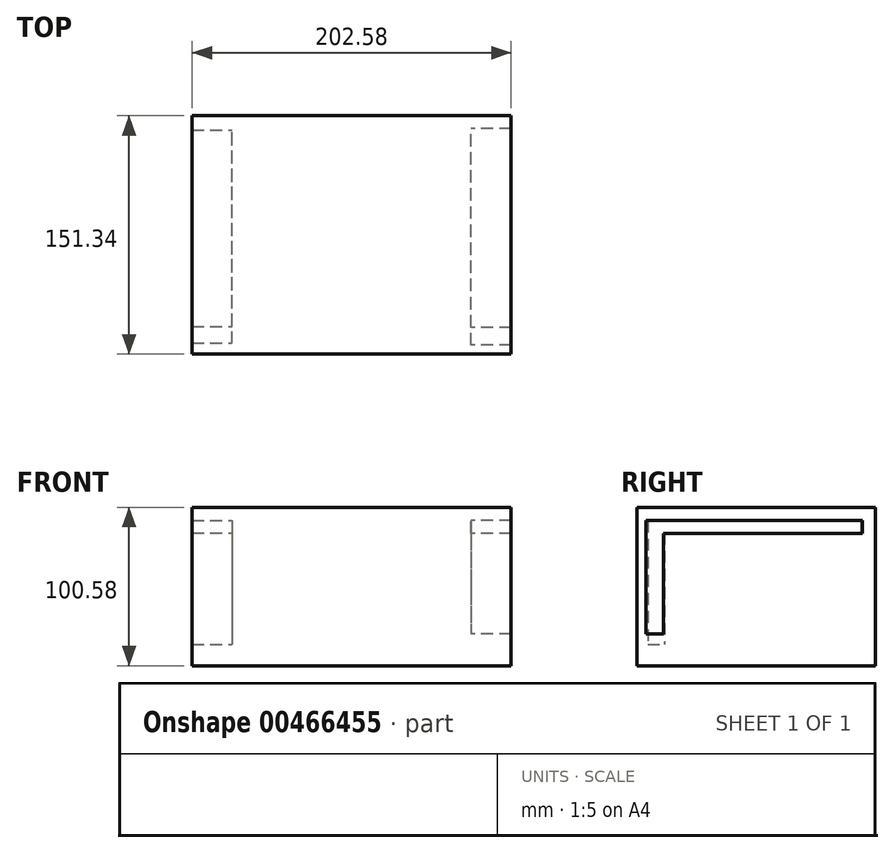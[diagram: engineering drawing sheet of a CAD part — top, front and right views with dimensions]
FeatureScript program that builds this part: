
annotation { "Feature Type Name" : "Feature", "Feature Type Description" : "" }
export const myFeature = defineFeature(function(context is Context, id is Id, definition is map)
    precondition{}
    {
        {
            var Q0;
            Q0=qCreatedBy(makeId("Top.planeOp"),FACE);
            var sketch = newSketch(context, id + "F0", { "sketchPlane" : qUnion([Q0])});
            skLineSegment(sketch, "E0.bottom", {"start": v(-76.71, -74.24) * mm, "end": v(75.07, -74.24) * mm});
            skLineSegment(sketch, "E0.top", {"start": v(-76.71, 77.1) * mm, "end": v(75.07, 77.1) * mm});
            skLineSegment(sketch, "E0.left", {"start": v(-76.71, -74.24) * mm, "end": v(-76.71, 77.1) * mm});
            skLineSegment(sketch, "E0.right", {"start": v(75.07, -74.24) * mm, "end": v(75.07, 77.1) * mm});
            skSolve(sketch);
        }
        {
            var Q0;
            Q0=makeQuery(id+"F0.imprint","IMPRINT",FACE,{"disambiguationData":[TD([[makeQuery(id+"F0.imprint","IMPRINT",EDGE,{"derivedFrom":sQuery(id+"F0.wireOp",EDGE,"E0.bottom")}),1.0]])]});
            extrude(context, id + "F1", {"entities" : qUnion([Q0]), "depth" : 100.58 * mm, "offsetDistance" : 25.4 * mm});
        }
        {
            var Q0;
            Q0=makeQuery(id+"F1.opExtrude","SWEPT_FACE",FACE,{"disambiguationData":[OSD([sQuery(id+"F0.wireOp",EDGE,"E0.right")])]});
            var sketch = newSketch(context, id + "F2", { "sketchPlane" : qUnion([Q0])});
            skLineSegment(sketch, "E1.bottom", {"start": v(-68.47, 84.2) * mm, "end": v(69.05, 84.2) * mm});
            skLineSegment(sketch, "E1.top", {"start": v(-68.47, 92.2) * mm, "end": v(69.05, 92.2) * mm});
            skLineSegment(sketch, "E1.left", {"start": v(-68.47, 84.2) * mm, "end": v(-68.47, 92.2) * mm});
            skLineSegment(sketch, "E1.right", {"start": v(69.05, 84.2) * mm, "end": v(69.05, 92.2) * mm});
            skLineSegment(sketch, "E2.bottom", {"start": v(-68.47, 92.2) * mm, "end": v(-57.37, 92.2) * mm});
            skLineSegment(sketch, "E2.top", {"start": v(-68.47, 20.36) * mm, "end": v(-57.37, 20.36) * mm});
            skLineSegment(sketch, "E2.left", {"start": v(-68.47, 92.2) * mm, "end": v(-68.47, 20.36) * mm});
            skLineSegment(sketch, "E2.right", {"start": v(-57.37, 92.2) * mm, "end": v(-57.37, 20.36) * mm});
            skSolve(sketch);
        }
        {
            var Q0;
            Q0=makeQuery(id+"F2.imprint","IMPRINT",FACE,{"disambiguationData":[TD([[makeQuery(id+"F2.imprint","IMPRINT",EDGE,{"derivedFrom":sQuery(id+"F2.wireOp",EDGE,"E1.top")}),1.0]])]});
            extrude(context, id + "F3", {"entities" : qUnion([Q0]), "operationType" : NewBodyOperationType.ADD, "depth" : 25.4 * mm, "offsetDistance" : 25.4 * mm});
        }
        {
            var Q0;
            Q0=makeQuery(id+"F1.opExtrude","SWEPT_FACE",FACE,{"disambiguationData":[OSD([sQuery(id+"F0.wireOp",EDGE,"E0.left")])]});
            var sketch = newSketch(context, id + "F4", { "sketchPlane" : qUnion([Q0])});
            skLineSegment(sketch, "E3.bottom", {"start": v(67.44, 92.2) * mm, "end": v(-67.93, 92.2) * mm});
            skLineSegment(sketch, "E3.top", {"start": v(67.44, 84.5) * mm, "end": v(-67.93, 84.5) * mm});
            skLineSegment(sketch, "E3.left", {"start": v(67.44, 92.2) * mm, "end": v(67.44, 84.5) * mm});
            skLineSegment(sketch, "E3.right", {"start": v(-67.93, 92.2) * mm, "end": v(-67.93, 84.5) * mm});
            skLineSegment(sketch, "E4.bottom", {"start": v(67.44, 92.2) * mm, "end": v(56.95, 92.2) * mm});
            skLineSegment(sketch, "E4.top", {"start": v(67.44, 13.58) * mm, "end": v(56.95, 13.58) * mm});
            skLineSegment(sketch, "E4.left", {"start": v(67.44, 92.2) * mm, "end": v(67.44, 13.58) * mm});
            skLineSegment(sketch, "E4.right", {"start": v(56.95, 92.2) * mm, "end": v(56.95, 13.58) * mm});
            skSolve(sketch);
        }
        {
            var Q0;
            Q0=makeQuery(id+"F4.imprint","IMPRINT",FACE,{"disambiguationData":[TD([[makeQuery(id+"F4.imprint","IMPRINT",EDGE,{"derivedFrom":sQuery(id+"F4.wireOp",EDGE,"E3.bottom")}),-1.0]])]});
            extrude(context, id + "F5", {"entities" : qUnion([Q0]), "operationType" : NewBodyOperationType.ADD, "depth" : 25.4 * mm, "offsetDistance" : 25.4 * mm});
        }
    });
